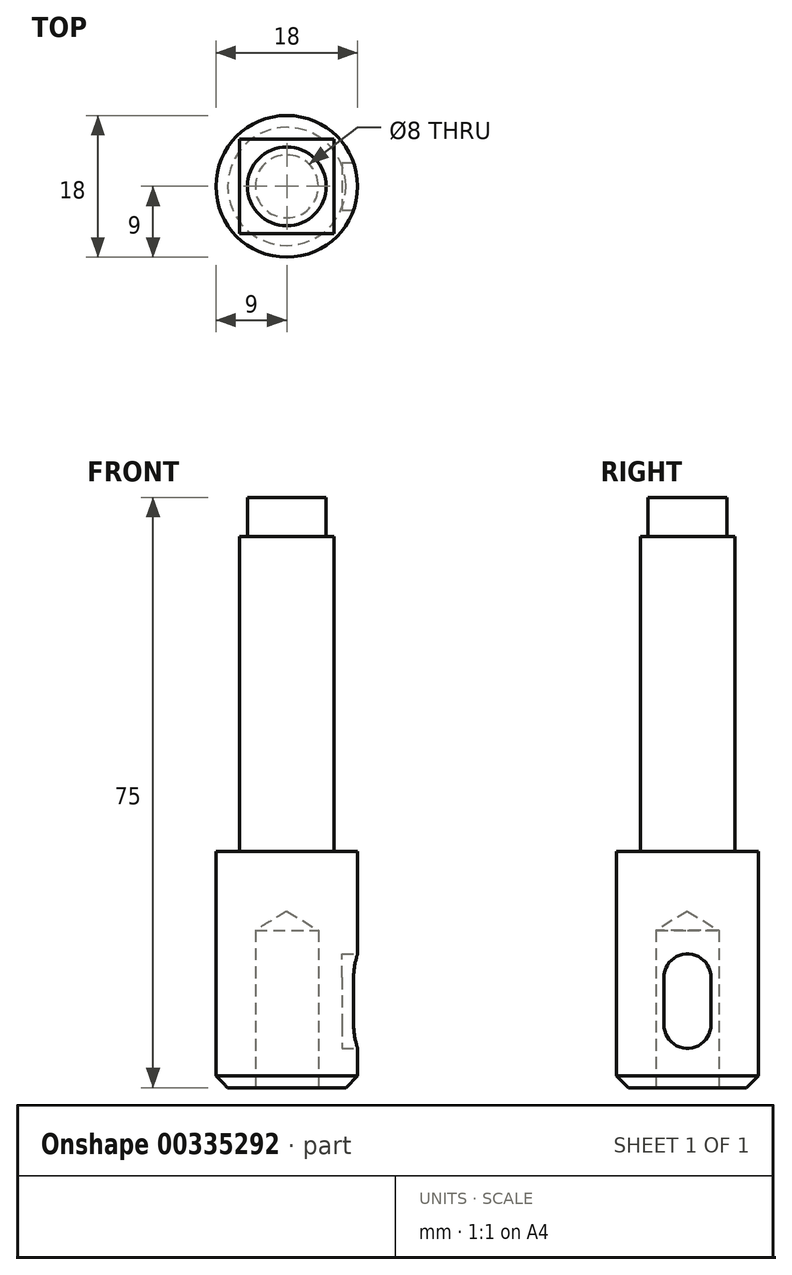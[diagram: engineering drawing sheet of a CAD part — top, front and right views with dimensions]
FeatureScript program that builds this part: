
annotation { "Feature Type Name" : "Feature", "Feature Type Description" : "" }
export const myFeature = defineFeature(function(context is Context, id is Id, definition is map)
    precondition{}
    {
        {
            var Q0;
            Q0=qCreatedBy(makeId("Top.planeOp"),FACE);
            var sketch = newSketch(context, id + "F0", { "sketchPlane" : qUnion([Q0])});
            skLineSegment(sketch, "E0.bottom", {"start": v(6, 6) * mm, "end": v(-6, 6) * mm});
            skLineSegment(sketch, "E0.top", {"start": v(6, -6) * mm, "end": v(-6, -6) * mm});
            skLineSegment(sketch, "E0.left", {"start": v(6, 6) * mm, "end": v(6, -6) * mm});
            skLineSegment(sketch, "E0.right", {"start": v(-6, 6) * mm, "end": v(-6, -6) * mm});
            skPoint(sketch, "E0.middle", {"position": v(0, 0) * mm});
            skSolve(sketch);
        }
        {
            var Q0;
            Q0=makeQuery(id+"F0.imprint","IMPRINT",FACE,{"disambiguationData":[TD([[makeQuery(id+"F0.imprint","IMPRINT",EDGE,{"derivedFrom":sQuery(id+"F0.wireOp",EDGE,"E0.bottom")}),1.0]])]});
            extrude(context, id + "F1", {"entities" : qUnion([Q0]), "depth" : 40 * mm, "symmetric" : true});
        }
        {
            var Q0;
            Q0=makeQuery(id+"F1.opExtrude","CAP_FACE",FACE,{"disambiguationData":[OSD([sQuery(id+"F0.wireOp",EDGE,"E0.bottom"),sQuery(id+"F0.wireOp",EDGE,"E0.top"),sQuery(id+"F0.wireOp",EDGE,"E0.left"),sQuery(id+"F0.wireOp",EDGE,"E0.right")])],"isStart":false});
            var sketch = newSketch(context, id + "F2", { "sketchPlane" : qUnion([Q0])});
            skCircle(sketch, "E1", {"center": v(0, 0) * mm, "radius": 5 * mm});
            skSolve(sketch);
        }
        {
            var Q0;
            Q0 = qSketchRegion(id + "F2", true);
            extrude(context, id + "F3", {"entities" : qUnion([Q0]), "operationType" : NewBodyOperationType.ADD, "depth" : 5 * mm});
        }
        {
            var Q0;
            Q0=makeQuery(id+"F1.opExtrude","CAP_FACE",FACE,{"disambiguationData":[OSD([sQuery(id+"F0.wireOp",EDGE,"E0.bottom"),sQuery(id+"F0.wireOp",EDGE,"E0.top"),sQuery(id+"F0.wireOp",EDGE,"E0.left"),sQuery(id+"F0.wireOp",EDGE,"E0.right")])],"isStart":true});
            var sketch = newSketch(context, id + "F4", { "sketchPlane" : qUnion([Q0])});
            skCircle(sketch, "E2", {"center": v(0, 0) * mm, "radius": 9 * mm});
            skSolve(sketch);
        }
        {
            var Q0;
            Q0 = qSketchRegion(id + "F4", true);
            extrude(context, id + "F5", {"entities" : qUnion([Q0]), "operationType" : NewBodyOperationType.ADD, "depth" : 30 * mm});
        }
        {
            var Q0;
            Q0=qCreatedBy(makeId("Right.planeOp"),FACE);
            cPlane(context, id + "F6", {"entities" : qUnion([Q0]), "cplaneType" : CPlaneType.OFFSET, "offset" : 9 * mm, "width" : 150 * mm, "height" : 150 * mm});
        }
        {
            var Q0;
            Q0=qCreatedBy(id+"F6.planeOp",FACE);
            var sketch = newSketch(context, id + "F7", { "sketchPlane" : qUnion([Q0])});
            skArc(sketch, "E3", {"start": v(-3, -42) * mm, "mid": v(0, -45) * mm, "end": v(3, -42) * mm});
            skArc(sketch, "E4", {"start": v(3, -36) * mm, "mid": v(0, -33) * mm, "end": v(-3, -36) * mm});
            skLineSegment(sketch, "E5", {"start": v(3, -36) * mm, "end": v(3, -42) * mm});
            skLineSegment(sketch, "E6", {"start": v(-3, -36) * mm, "end": v(-3, -42) * mm});
            skSolve(sketch);
        }
        {
            var Q0;
            Q0=makeQuery(id+"F7.imprint","IMPRINT",FACE,{"disambiguationData":[TD([[makeQuery(id+"F7.imprint","IMPRINT",EDGE,{"derivedFrom":sQuery(id+"F7.wireOp",EDGE,"E3")}),1.0]])]});
            extrude(context, id + "F8", {"entities" : qUnion([Q0]), "operationType" : NewBodyOperationType.REMOVE, "oppositeDirection" : true, "depth" : 2 * mm});
        }
        {
            var Q0;
            Q0=makeQuery(id+"F5.opExtrude","CAP_FACE",FACE,{"disambiguationData":[OSD([sQuery(id+"F4.wireOp",EDGE,"E2")])],"isStart":false});
            var sketch = newSketch(context, id + "F9", { "sketchPlane" : qUnion([Q0])});
            skPoint(sketch, "E7", {"position": v(0, 0) * mm});
            skSolve(sketch);
        }
        {
            var Q0;
            Q0=sQuery(id+"F9.wireOp",VERTEX,"E7");
            var Q1;
            Q1=makeQuery(id+"F1.opExtrude","SWEPT_BODY",BODY,{"disambiguationData":[OSD([sQuery(id+"F0.wireOp",EDGE,"E0.bottom"),sQuery(id+"F0.wireOp",EDGE,"E0.top"),sQuery(id+"F0.wireOp",EDGE,"E0.left"),sQuery(id+"F0.wireOp",EDGE,"E0.right")])]});
            hole(context, id + "F10", {"style" : HoleStyle.SIMPLE, "endStyle" : HoleEndStyle.BLIND, "holeDiameter" : 8 * mm, "holeDepth" : 20 * mm, "tappedDepth" : 12 * mm, "tapClearance" : 3, "startFromSketch" : true, "locations" : qUnion([Q0]), "scope" : qUnion([Q1])});
        }
        {
            var Q0;
            Q0=makeQuery(id+"F5.opExtrude","CAP_EDGE",EDGE,{"disambiguationData":[OSD([sQuery(id+"F4.wireOp",EDGE,"E2")])],"isStart":false});
            chamfer(context, id + "F11", {"entities" : qUnion([Q0]), "width" : 1.5 * mm, "tangentPropagation" : true});
        }
    });
